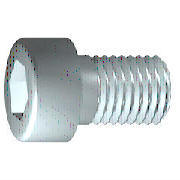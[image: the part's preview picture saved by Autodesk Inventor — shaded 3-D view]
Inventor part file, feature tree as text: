
AUTODESK INVENTOR PART (.ipt)
format: ipt  version: 2012 (Build 160160000, 160)  size: 191,488 bytes
history: native  units: mm (DEFAULTED — no unit token found)
features: extrude x1, plane x1, fillet x1
ambient origin geometry x7: Origin, YZ Plane, XY Plane, X Axis, Y Axis, Z Axis, Center Point
bodies: Solid1 (feature_tree), Body (feature_tree)
feature tree (3):
  extrude  "Slot"  Depth=5.026968mm
  plane  "Work Plane1"
  fillet  "Fillet2"  Radius=1.322932mm
